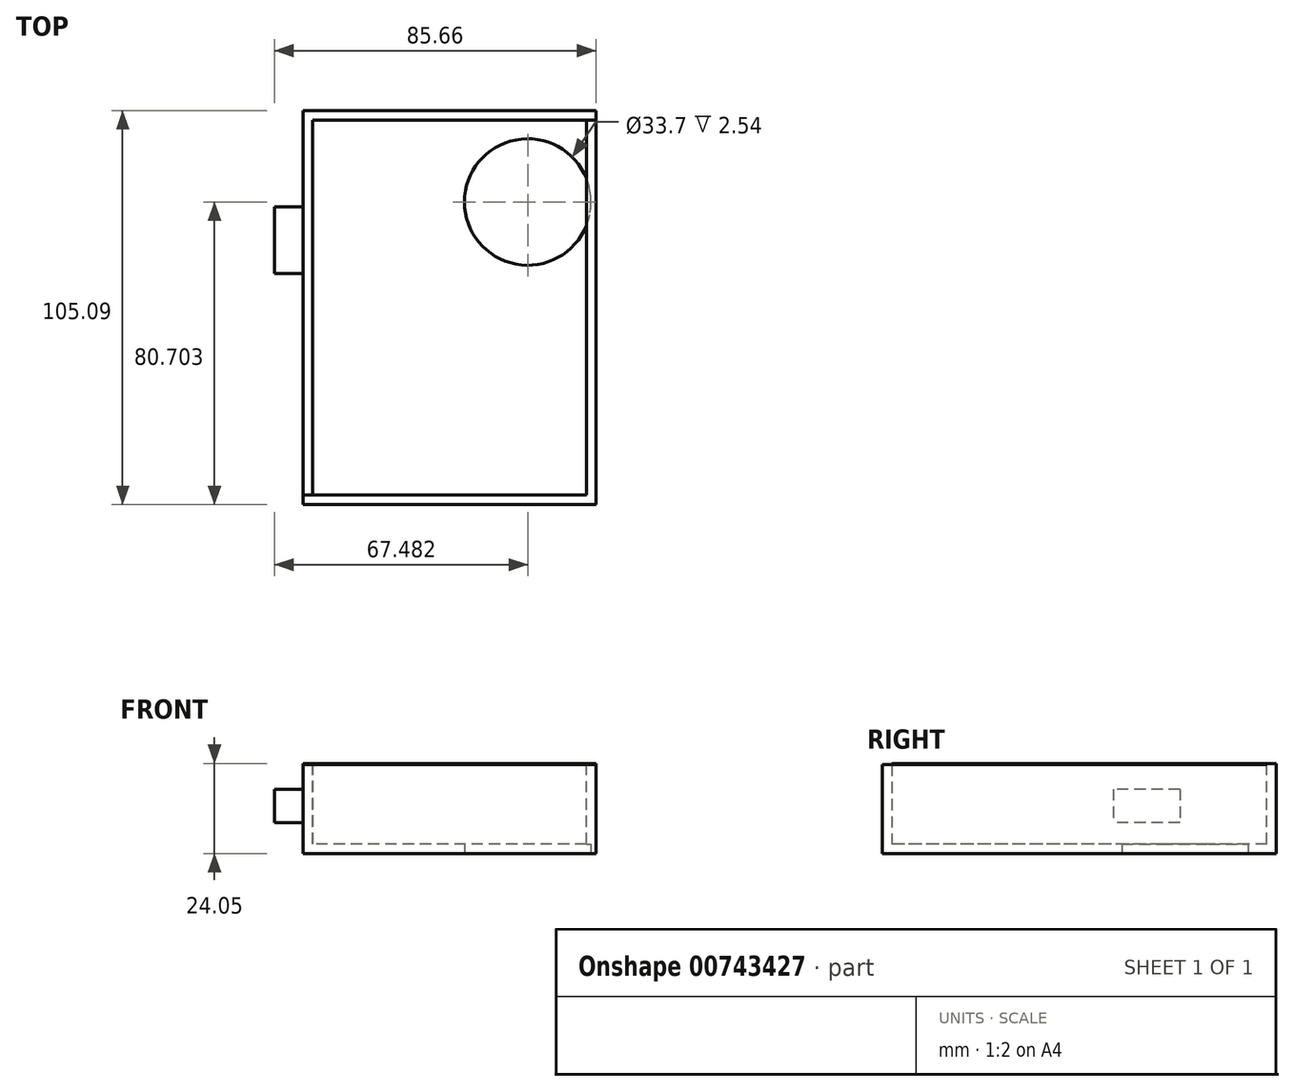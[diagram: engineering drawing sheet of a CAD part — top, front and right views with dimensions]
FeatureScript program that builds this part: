
annotation { "Feature Type Name" : "Feature", "Feature Type Description" : "" }
export const myFeature = defineFeature(function(context is Context, id is Id, definition is map)
    precondition{}
    {
        {
            var Q0;
            Q0=qCreatedBy(makeId("Top.planeOp"),FACE);
            var sketch = newSketch(context, id + "F0", { "sketchPlane" : qUnion([Q0])});
            skLineSegment(sketch, "E0.bottom", {"start": v(58.53, 63.63) * mm, "end": v(-19.51, 63.63) * mm});
            skLineSegment(sketch, "E0.top", {"start": v(58.53, -41.46) * mm, "end": v(-19.51, -41.46) * mm});
            skLineSegment(sketch, "E0.left", {"start": v(58.53, 63.63) * mm, "end": v(58.53, -41.46) * mm});
            skLineSegment(sketch, "E0.right", {"start": v(-19.51, 63.63) * mm, "end": v(-19.51, -41.46) * mm});
            skCircle(sketch, "E1", {"center": v(40.35, 39.24) * mm, "radius": 16.85 * mm});
            skSolve(sketch);
        }
        {
            var Q0;
            Q0=makeQuery(id+"F0.imprint","IMPRINT",FACE,{"disambiguationData":[TD([[makeQuery(id+"F0.imprint","IMPRINT",EDGE,{"derivedFrom":sQuery(id+"F0.wireOp",EDGE,"E0.bottom")}),1.0]])]});
            extrude(context, id + "F1", {"entities" : qUnion([Q0]), "depth" : 2.54 * mm, "offsetDistance" : 25.4 * mm});
        }
        {
            var Q0;
            Q0=makeQuery(id+"F1.opExtrude","SWEPT_FACE",FACE,{"disambiguationData":[OSD([sQuery(id+"F0.wireOp",EDGE,"E0.bottom")])]});
            var sketch = newSketch(context, id + "F2", { "sketchPlane" : qUnion([Q0])});
            skLineSegment(sketch, "E2", {"start": v(-58.53, 2.54) * mm, "end": v(-58.53, 24.05) * mm});
            skLineSegment(sketch, "E3.bottom", {"start": v(-58.53, 24.05) * mm, "end": v(19.51, 24.05) * mm});
            skLineSegment(sketch, "E3.top", {"start": v(-58.53, 2.54) * mm, "end": v(19.51, 2.54) * mm});
            skLineSegment(sketch, "E3.left", {"start": v(-58.53, 24.05) * mm, "end": v(-58.53, 2.54) * mm});
            skLineSegment(sketch, "E3.right", {"start": v(19.51, 24.05) * mm, "end": v(19.51, 2.54) * mm});
            skSolve(sketch);
        }
        {
            var Q0;
            Q0=makeQuery(id+"F2.imprint","IMPRINT",FACE,{"disambiguationData":[TD([[makeQuery(id+"F2.imprint","IMPRINT",EDGE,{"derivedFrom":sQuery(id+"F2.wireOp",EDGE,"E3.bottom")}),-1.0]])]});
            extrude(context, id + "F3", {"entities" : qUnion([Q0]), "operationType" : NewBodyOperationType.ADD, "depth" : -2.54 * mm, "offsetDistance" : 25.4 * mm});
        }
        {
            var Q0;
            Q0=makeQuery(id+"F1.opExtrude","SWEPT_FACE",FACE,{"disambiguationData":[OSD([sQuery(id+"F0.wireOp",EDGE,"E0.top")])]});
            var sketch = newSketch(context, id + "F4", { "sketchPlane" : qUnion([Q0])});
            skLineSegment(sketch, "E4", {"start": v(-19.51, 2.54) * mm, "end": v(-19.51, 23.76) * mm});
            skLineSegment(sketch, "E5.bottom", {"start": v(-19.51, 23.76) * mm, "end": v(58.53, 23.76) * mm});
            skLineSegment(sketch, "E5.top", {"start": v(-19.51, 2.54) * mm, "end": v(58.53, 2.54) * mm});
            skLineSegment(sketch, "E5.left", {"start": v(-19.51, 23.76) * mm, "end": v(-19.51, 2.54) * mm});
            skLineSegment(sketch, "E5.right", {"start": v(58.53, 23.76) * mm, "end": v(58.53, 2.54) * mm});
            skSolve(sketch);
        }
        {
            var Q0;
            Q0 = qSketchRegion(id + "F4", true);
            extrude(context, id + "F5", {"entities" : qUnion([Q0]), "operationType" : NewBodyOperationType.ADD, "depth" : -2.54 * mm, "offsetDistance" : 25.4 * mm});
        }
        {
            var Q0;
            Q0=makeQuery(id+"F5.boolean.opBoolean","MERGE",FACE,{"derivedFrom":[makeQuery(id+"F3.boolean.opBoolean","MERGE",FACE,{"derivedFrom":[makeQuery(id+"F1.opExtrude","SWEPT_FACE",FACE,{"disambiguationData":[OSD([sQuery(id+"F0.wireOp",EDGE,"E0.right")])]}),makeQuery(id+"F3.opExtrude","SWEPT_FACE",FACE,{"disambiguationData":[OSD([sQuery(id+"F2.wireOp",EDGE,"E3.right")])]})]}),makeQuery(id+"F5.opExtrude","SWEPT_FACE",FACE,{"disambiguationData":[OSD([sQuery(id+"F4.wireOp",EDGE,"E5.left")])]})]});
            var sketch = newSketch(context, id + "F6", { "sketchPlane" : qUnion([Q0])});
            skLineSegment(sketch, "E6.bottom", {"start": v(-61.1, 24.05) * mm, "end": v(38.92, 24.05) * mm});
            skLineSegment(sketch, "E6.top", {"start": v(-61.1, 2.54) * mm, "end": v(38.92, 2.54) * mm});
            skLineSegment(sketch, "E6.left", {"start": v(-61.1, 24.05) * mm, "end": v(-61.1, 2.54) * mm});
            skLineSegment(sketch, "E6.right", {"start": v(38.92, 24.05) * mm, "end": v(38.92, 2.54) * mm});
            skSolve(sketch);
        }
        {
            var Q0;
            {var subQ2=sQuery(id+"F6.wireOp",EDGE,"E6.bottom");Q0=makeQuery(id+"F6.imprint","IMPRINT",FACE,{"disambiguationData":[TD([[makeQuery(id+"F6.imprint","IMPRINT",EDGE,{"derivedFrom":subQ2}),-1.0]])]});}
            extrude(context, id + "F7", {"entities" : qUnion([Q0]), "operationType" : NewBodyOperationType.ADD, "depth" : -2.54 * mm, "offsetDistance" : 25.4 * mm});
        }
        {
            var Q0;
            Q0=makeQuery(id+"F5.boolean.opBoolean","MERGE",FACE,{"derivedFrom":[makeQuery(id+"F3.boolean.opBoolean","MERGE",FACE,{"derivedFrom":[makeQuery(id+"F1.opExtrude","SWEPT_FACE",FACE,{"disambiguationData":[OSD([sQuery(id+"F0.wireOp",EDGE,"E0.left")])]}),makeQuery(id+"F3.opExtrude","SWEPT_FACE",FACE,{"disambiguationData":[OSD([sQuery(id+"F2.wireOp",EDGE,"E3.left")])]})]}),makeQuery(id+"F5.opExtrude","SWEPT_FACE",FACE,{"disambiguationData":[OSD([sQuery(id+"F4.wireOp",EDGE,"E5.right")])]})]});
            var sketch = newSketch(context, id + "F8", { "sketchPlane" : qUnion([Q0])});
            skLineSegment(sketch, "E7.bottom", {"start": v(-38.92, 23.76) * mm, "end": v(61.1, 23.76) * mm});
            skLineSegment(sketch, "E7.top", {"start": v(-38.92, 2.54) * mm, "end": v(61.1, 2.54) * mm});
            skLineSegment(sketch, "E7.left", {"start": v(-38.92, 23.76) * mm, "end": v(-38.92, 2.54) * mm});
            skLineSegment(sketch, "E7.right", {"start": v(61.1, 23.76) * mm, "end": v(61.1, 2.54) * mm});
            skSolve(sketch);
        }
        {
            var Q0;
            Q0=makeQuery(id+"F8.imprint","IMPRINT",FACE,{"disambiguationData":[TD([[makeQuery(id+"F8.imprint","IMPRINT",EDGE,{"derivedFrom":sQuery(id+"F8.wireOp",EDGE,"E7.bottom")}),-1.0]])]});
            extrude(context, id + "F9", {"entities" : qUnion([Q0]), "operationType" : NewBodyOperationType.ADD, "depth" : -2.54 * mm, "offsetDistance" : 25.4 * mm});
        }
        {
            var Q0;
            Q0=makeQuery(id+"F7.boolean.opBoolean","MERGE",FACE,{"derivedFrom":[makeQuery(id+"F5.boolean.opBoolean","MERGE",FACE,{"derivedFrom":[makeQuery(id+"F3.boolean.opBoolean","MERGE",FACE,{"derivedFrom":[makeQuery(id+"F1.opExtrude","SWEPT_FACE",FACE,{"disambiguationData":[OSD([sQuery(id+"F0.wireOp",EDGE,"E0.right")])]}),makeQuery(id+"F3.opExtrude","SWEPT_FACE",FACE,{"disambiguationData":[OSD([sQuery(id+"F2.wireOp",EDGE,"E3.right")])]})]}),makeQuery(id+"F5.opExtrude","SWEPT_FACE",FACE,{"disambiguationData":[OSD([sQuery(id+"F4.wireOp",EDGE,"E5.left")])]})]}),makeQuery(id+"F7.opExtrude","CAP_FACE",FACE,{"disambiguationData":[OSD([sQuery(id+"F6.wireOp",EDGE,"E6.bottom"),sQuery(id+"F6.wireOp",EDGE,"E6.top"),sQuery(id+"F6.wireOp",EDGE,"E6.left"),sQuery(id+"F6.wireOp",EDGE,"E6.right")])],"isStart":true})]});
            var sketch = newSketch(context, id + "F10", { "sketchPlane" : qUnion([Q0])});
            skLineSegment(sketch, "E8.bottom", {"start": v(-37.93, 17.18) * mm, "end": v(-20.18, 17.18) * mm});
            skLineSegment(sketch, "E8.top", {"start": v(-37.93, 8.3) * mm, "end": v(-20.18, 8.3) * mm});
            skLineSegment(sketch, "E8.left", {"start": v(-37.93, 17.18) * mm, "end": v(-37.93, 8.3) * mm});
            skLineSegment(sketch, "E8.right", {"start": v(-20.18, 17.18) * mm, "end": v(-20.18, 8.3) * mm});
            skSolve(sketch);
        }
        {
            var Q0;
            Q0=makeQuery(id+"F10.imprint","IMPRINT",FACE,{"disambiguationData":[TD([[makeQuery(id+"F10.imprint","IMPRINT",EDGE,{"derivedFrom":sQuery(id+"F10.wireOp",EDGE,"E8.bottom")}),-1.0]])]});
            extrude(context, id + "F11", {"entities" : qUnion([Q0]), "operationType" : NewBodyOperationType.ADD, "depth" : 7.62 * mm, "offsetDistance" : 25.4 * mm});
        }
    });
